# Revit family: GRAS_HW-25N-20-30 SH
name_source: partatom
category: Osprzęt hydrauliczny
revit_build: Autodesk Revit 2018 (Build: 20190510_1515(x64)
units: mm (PartAtom-declared; Revit-internal decimal feet)

## family parameters
Obiekt nadrzędny = Powierzchnia
Punkt obliczania pomieszczeń = Nie
Tnij formami wycięć po wczytaniu = Nie
Typ części = Normalny
Współdzielony = Nie
Wymiar okrągłego złącza = Użyj średnicy

## types (2) — shared parameters
Cabinet depth = 250 mm  [stored 0.82021 ft]
Cabinet height = 790 mm  [stored 2.59186 ft]
Cabinet width = 740 mm  [stored 2.42782 ft]
D = 100 mm  [stored 0.328084 ft]
DN = 25 mm  [stored 0.082021 ft]
Flow = 60.0 L/s
H = 100 mm  [stored 0.328084 ft]
K Factor = 42
Producent = GRAS PPPH
URL = https://gras.pl
W = 100 mm  [stored 0.328084 ft]
zero-valued in all types: Domyślna rzędna

## per-type parameters (varying)
| type | Cabinet material |
| HW-25N-20/30 SH, RAL3000 | DC01, RAL3000 |
| HW-25N-20/30 SH, RAL9010 | DC01, RAL9010 |

note: column(s) folded — value = type name in every type: Model

note: [stored X ft] marks values corroborated as IEEE doubles in the binary element streams (Revit-internal decimal feet)

## geometry (parser evidence)
native form markers: Blend x4
no freeform markers — native parametric forms only
